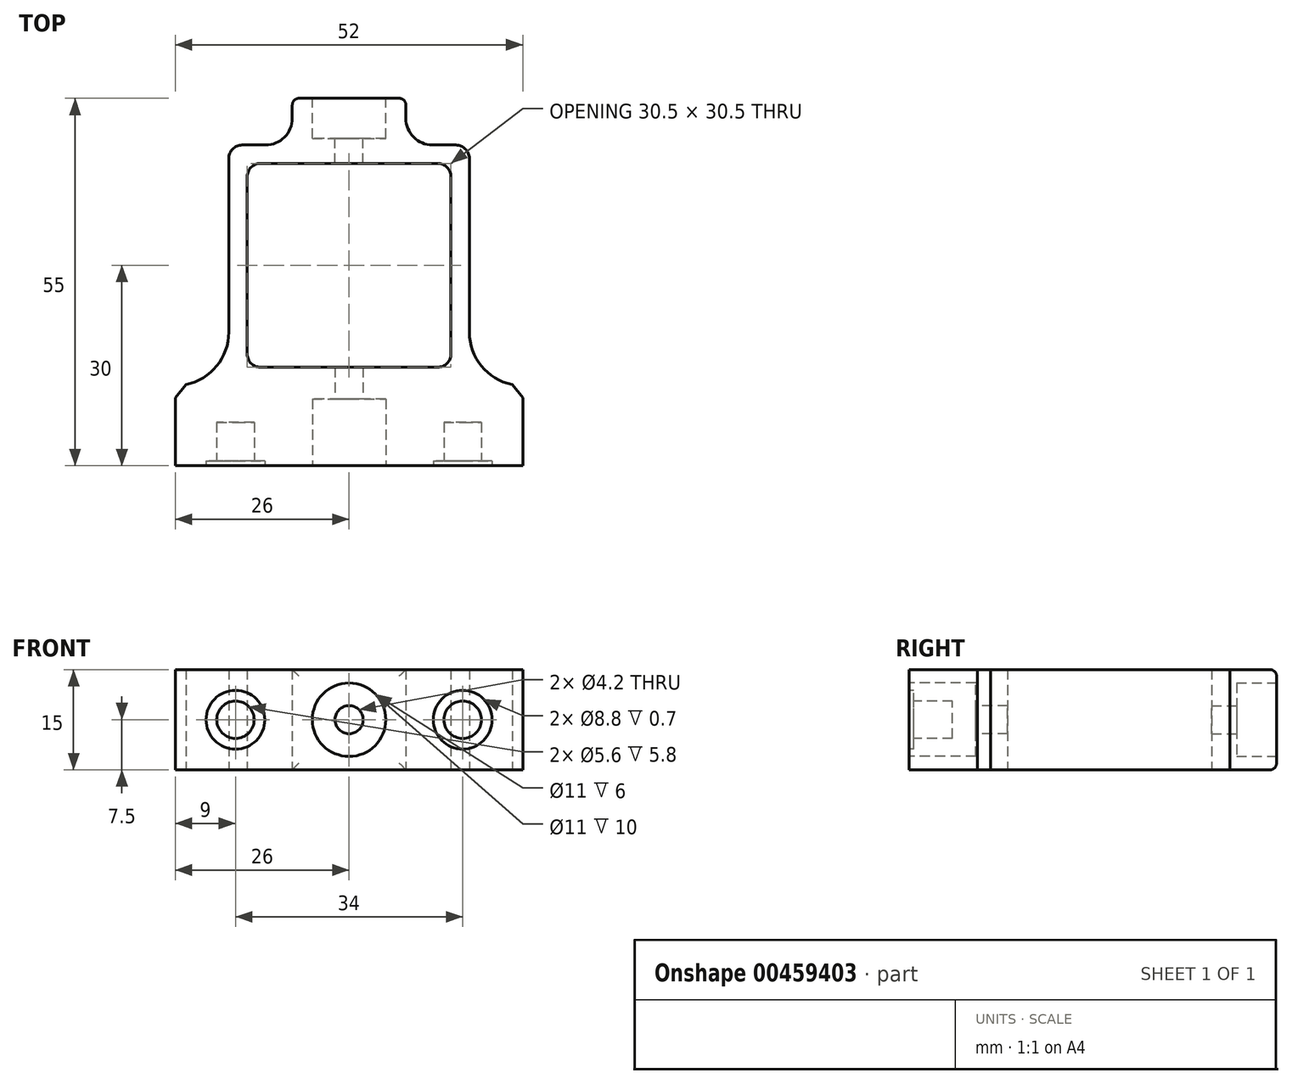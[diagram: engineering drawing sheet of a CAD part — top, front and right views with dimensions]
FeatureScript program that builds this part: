
annotation { "Feature Type Name" : "Feature", "Feature Type Description" : "" }
export const myFeature = defineFeature(function(context is Context, id is Id, definition is map)
    precondition{}
    {
        {
            var Q0;
            Q0=qCreatedBy(makeId("Top.planeOp"),FACE);
            var sketch = newSketch(context, id + "F0", { "sketchPlane" : qUnion([Q0])});
            skLineSegment(sketch, "E0.bottom", {"start": v(13.25, 15.25) * mm, "end": v(-13.25, 15.25) * mm});
            skLineSegment(sketch, "E0.top", {"start": v(13.25, -15.25) * mm, "end": v(-13.25, -15.25) * mm});
            skLineSegment(sketch, "E0.left", {"start": v(15.25, 13.25) * mm, "end": v(15.25, -13.25) * mm});
            skLineSegment(sketch, "E0.right", {"start": v(-15.25, 13.25) * mm, "end": v(-15.25, -13.25) * mm});
            skPoint(sketch, "E0.middle", {"position": v(0, 0) * mm});
            skPoint(sketch, "E1.visualSharp", {"position": v(-15.25, 15.25) * mm});
            skArc(sketch, "E1.filletArc", {"start": v(-13.25, 15.25) * mm, "mid": v(-14.66, 14.66) * mm, "end": v(-15.25, 13.25) * mm});
            skPoint(sketch, "E2.visualSharp", {"position": v(15.25, 15.25) * mm});
            skArc(sketch, "E2.filletArc", {"start": v(15.25, 13.25) * mm, "mid": v(14.66, 14.66) * mm, "end": v(13.25, 15.25) * mm});
            skPoint(sketch, "E3.visualSharp", {"position": v(15.25, -15.25) * mm});
            skArc(sketch, "E3.filletArc", {"start": v(13.25, -15.25) * mm, "mid": v(14.66, -14.66) * mm, "end": v(15.25, -13.25) * mm});
            skPoint(sketch, "E4.visualSharp", {"position": v(-15.25, -15.25) * mm});
            skArc(sketch, "E4.filletArc", {"start": v(-15.25, -13.25) * mm, "mid": v(-14.66, -14.66) * mm, "end": v(-13.25, -15.25) * mm});
            skLineSegment(sketch, "E5.bottom", {"start": v(16, 18) * mm, "end": v(12.5, 18) * mm});
            skLineSegment(sketch, "E5.left", {"start": v(18, 16) * mm, "end": v(18, -10) * mm});
            skLineSegment(sketch, "E5.right", {"start": v(-18, 16) * mm, "end": v(-18, -10) * mm});
            skPoint(sketch, "E6.visualSharp", {"position": v(-18, 18) * mm});
            skArc(sketch, "E6.filletArc", {"start": v(-16, 18) * mm, "mid": v(-17.41, 17.41) * mm, "end": v(-18, 16) * mm});
            skPoint(sketch, "E7.visualSharp", {"position": v(18, 18) * mm});
            skArc(sketch, "E7.filletArc", {"start": v(18, 16) * mm, "mid": v(17.41, 17.41) * mm, "end": v(16, 18) * mm});
            skLineSegment(sketch, "E8.bottom", {"start": v(-26, -18) * mm, "end": v(-26, -18) * mm});
            skLineSegment(sketch, "E8.top", {"start": v(-26, -30) * mm, "end": v(26, -30) * mm});
            skLineSegment(sketch, "E8.left", {"start": v(-26, -18) * mm, "end": v(-26, -30) * mm});
            skLineSegment(sketch, "E8.right", {"start": v(26, -18) * mm, "end": v(26, -30) * mm});
            skLineSegment(sketch, "E9.trimOffspring", {"start": v(26, -18) * mm, "end": v(26, -18) * mm});
            skPoint(sketch, "E10.visualSharp", {"position": v(-18, -18) * mm});
            skArc(sketch, "E10.filletArc", {"start": v(-26, -18) * mm, "mid": v(-20.34, -15.66) * mm, "end": v(-18, -10) * mm});
            skPoint(sketch, "E11.visualSharp", {"position": v(18, -18) * mm});
            skArc(sketch, "E11.filletArc", {"start": v(18, -10) * mm, "mid": v(20.34, -15.66) * mm, "end": v(26, -18) * mm});
            skLineSegment(sketch, "E12.top", {"start": v(-8.5, 25) * mm, "end": v(8.5, 25) * mm});
            skLineSegment(sketch, "E12.left", {"start": v(-8.5, 22) * mm, "end": v(-8.5, 25) * mm});
            skLineSegment(sketch, "E12.right", {"start": v(8.5, 22) * mm, "end": v(8.5, 25) * mm});
            skLineSegment(sketch, "E13.trimOffspring", {"start": v(-12.5, 18) * mm, "end": v(-16, 18) * mm});
            skPoint(sketch, "E14.visualSharp", {"position": v(-8.5, 18) * mm});
            skArc(sketch, "E14.filletArc", {"start": v(-12.5, 18) * mm, "mid": v(-9.67, 19.17) * mm, "end": v(-8.5, 22) * mm});
            skPoint(sketch, "E15.visualSharp", {"position": v(8.5, 18) * mm});
            skArc(sketch, "E15.filletArc", {"start": v(8.5, 22) * mm, "mid": v(9.67, 19.17) * mm, "end": v(12.5, 18) * mm});
            skSolve(sketch);
        }
        {
            var Q0;
            Q0 = qSketchRegion(id + "F0", true);
            extrude(context, id + "F1", {"entities" : qUnion([Q0]), "depth" : 15 * mm});
        }
        {
            var Q0;
            Q0=makeQuery(id+"F1.opExtrude","SWEPT_EDGE",EDGE,{"disambiguationData":[OSD([sQuery(id+"F0.wireOp",EDGE,"E8.left"),sQuery(id+"F0.wireOp",EDGE,"E10.filletArc")])]});
            var Q1;
            Q1=makeQuery(id+"F1.opExtrude","SWEPT_EDGE",EDGE,{"disambiguationData":[OSD([sQuery(id+"F0.wireOp",EDGE,"E8.right"),sQuery(id+"F0.wireOp",EDGE,"E11.filletArc")])]});
            chamfer(context, id + "F2", {"entities" : qUnion([Q0, Q1]), "width" : 2 * mm, "tangentPropagation" : true});
        }
        {
            var Q0;
            Q0=makeQuery(id+"F1.opExtrude","SWEPT_FACE",FACE,{"disambiguationData":[OSD([sQuery(id+"F0.wireOp",EDGE,"E8.top")])]});
            var sketch = newSketch(context, id + "F3", { "sketchPlane" : qUnion([Q0])});
            skCircle(sketch, "E16", {"center": v(-17, 7.5) * mm, "radius": 2.8 * mm});
            skPoint(sketch, "E16.centerSnap0", {"position": v(-26, 7.5) * mm});
            skCircle(sketch, "E17", {"center": v(17, 7.5) * mm, "radius": 2.8 * mm});
            skSolve(sketch);
        }
        {
            var Q0;
            Q0=makeQuery(id+"F1.opExtrude","SWEPT_FACE",FACE,{"disambiguationData":[OSD([sQuery(id+"F0.wireOp",EDGE,"E12.top")])]});
            var sketch = newSketch(context, id + "F4", { "sketchPlane" : qUnion([Q0])});
            skCircle(sketch, "E18", {"center": v(0, 7.5) * mm, "radius": 5.5 * mm});
            skPoint(sketch, "E18.centerSnap0", {"position": v(-8.5, 7.5) * mm});
            skSolve(sketch);
        }
        {
            var Q0;
            Q0 = qSketchRegion(id + "F4", true);
            extrude(context, id + "F5", {"entities" : qUnion([Q0]), "operationType" : NewBodyOperationType.REMOVE, "oppositeDirection" : true, "depth" : 6 * mm});
        }
        {
            var Q0;
            Q0=makeQuery(id+"F1.opExtrude","CAP_EDGE",EDGE,{"disambiguationData":[OSD([sQuery(id+"F0.wireOp",EDGE,"E12.top")])],"isStart":true});
            var Q1;
            Q1=makeQuery(id+"F1.opExtrude","SWEPT_EDGE",EDGE,{"disambiguationData":[OSD([sQuery(id+"F0.wireOp",EDGE,"E12.top"),sQuery(id+"F0.wireOp",EDGE,"E12.left")])]});
            var Q2;
            Q2=makeQuery(id+"F1.opExtrude","CAP_EDGE",EDGE,{"disambiguationData":[OSD([sQuery(id+"F0.wireOp",EDGE,"E12.top")])],"isStart":false});
            var Q3;
            Q3=makeQuery(id+"F1.opExtrude","SWEPT_EDGE",EDGE,{"disambiguationData":[OSD([sQuery(id+"F0.wireOp",EDGE,"E12.top"),sQuery(id+"F0.wireOp",EDGE,"E12.right")])]});
            fillet(context, id + "F6", {"entities" : qUnion([Q0, Q1, Q2, Q3]), "radius" : 1 * mm, "tangentPropagation" : true, "allowEdgeOverflow" : false});
        }
        {
            var Q0;
            Q0=makeQuery(id+"F5.boolean.opBoolean","COPY",FACE,{"derivedFrom":makeQuery(id+"F5.opExtrude","CAP_FACE",FACE,{"disambiguationData":[OSD([sQuery(id+"F4.wireOp",EDGE,"E18")])],"isStart":false})});
            var sketch = newSketch(context, id + "F7", { "sketchPlane" : qUnion([Q0])});
            skCircle(sketch, "E19", {"center": v(0, 7.5) * mm, "radius": 2.1 * mm});
            skSolve(sketch);
        }
        {
            var Q0;
            Q0 = qSketchRegion(id + "F7", true);
            extrude(context, id + "F8", {"entities" : qUnion([Q0]), "operationType" : NewBodyOperationType.REMOVE, "endBound" : BoundingType.UP_TO_NEXT, "oppositeDirection" : true, "depth" : 25 * mm});
        }
        {
            var Q0;
            Q0=makeQuery(id+"F3.imprint","IMPRINT",FACE,{"disambiguationData":[TD([[makeQuery(id+"F3.imprint","IMPRINT",EDGE,{"derivedFrom":sQuery(id+"F3.wireOp",EDGE,"E16")}),-1.0]])]});
            var sketch = newSketch(context, id + "F9", { "sketchPlane" : qUnion([Q0])});
            skCircle(sketch, "E20", {"center": v(0, 7.5) * mm, "radius": 5.5 * mm});
            skSolve(sketch);
        }
        {
            var Q0;
            Q0 = qSketchRegion(id + "F9", true);
            var Q1;
            Q1=makeQuery(id+"F1.opExtrude","SWEPT_FACE",FACE,{"disambiguationData":[OSD([sQuery(id+"F0.wireOp",EDGE,"E0.top")])]});
            extrude(context, id + "F10", {"entities" : qUnion([Q0]), "operationType" : NewBodyOperationType.REMOVE, "oppositeDirection" : true, "endBoundEntityFace" : qUnion([Q1]), "depth" : 10 * mm, "hasSecondDirection" : true, "secondDirectionOppositeDirection" : false, "secondDirectionDepth" : 25 * mm});
        }
        {
            var Q0;
            Q0=makeQuery(id+"F3.imprint","IMPRINT",FACE,{"disambiguationData":[TD([[makeQuery(id+"F3.imprint","IMPRINT",EDGE,{"derivedFrom":sQuery(id+"F3.wireOp",EDGE,"E16")}),-1.0]])]});
            var sketch = newSketch(context, id + "F11", { "sketchPlane" : qUnion([Q0])});
            skCircle(sketch, "E21", {"center": v(0, 7.5) * mm, "radius": 2.1 * mm});
            skSolve(sketch);
        }
        {
            var Q0;
            Q0 = qSketchRegion(id + "F11", true);
            var Q1;
            Q1=makeQuery(id+"F1.opExtrude","SWEPT_FACE",FACE,{"disambiguationData":[OSD([sQuery(id+"F0.wireOp",EDGE,"E0.top")])]});
            extrude(context, id + "F12", {"entities" : qUnion([Q0]), "operationType" : NewBodyOperationType.REMOVE, "endBound" : BoundingType.UP_TO_SURFACE, "oppositeDirection" : true, "endBoundEntityFace" : qUnion([Q1]), "depth" : 25 * mm});
        }
        {
            var Q0;
            Q0 = qSketchRegion(id + "F3", true);
            extrude(context, id + "F13", {"entities" : qUnion([Q0]), "operationType" : NewBodyOperationType.REMOVE, "oppositeDirection" : true, "depth" : 6.5 * mm});
        }
        {
            var Q0;
            Q0=makeQuery(id+"F1.opExtrude","SWEPT_FACE",FACE,{"disambiguationData":[OSD([sQuery(id+"F0.wireOp",EDGE,"E8.top")])]});
            var sketch = newSketch(context, id + "F14", { "sketchPlane" : qUnion([Q0])});
            skCircle(sketch, "E22", {"center": v(17, 7.5) * mm, "radius": 4.4 * mm});
            skCircle(sketch, "E23", {"center": v(-17, 7.5) * mm, "radius": 4.4 * mm});
            skSolve(sketch);
        }
        {
            var Q0;
            Q0 = qSketchRegion(id + "F14", true);
            extrude(context, id + "F15", {"entities" : qUnion([Q0]), "operationType" : NewBodyOperationType.REMOVE, "oppositeDirection" : true, "depth" : 0.7 * mm});
        }
    });
